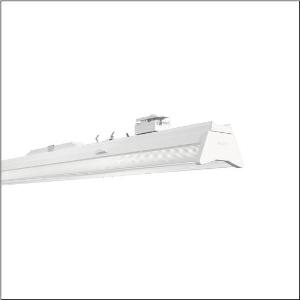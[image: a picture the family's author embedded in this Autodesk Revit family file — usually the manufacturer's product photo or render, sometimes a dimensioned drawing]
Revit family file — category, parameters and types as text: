
# Revit family: licross_r__11_performance_tw_51tm16tnt85x_6a4e
name_source: partatom
category: Lighting Fixtures
units: mm (PartAtom-declared; Revit-internal decimal feet)

## family parameters
Cut with Voids When Loaded = No
Host = Face
Light Source = No
Part Type = Normal
Room Calculation Point = No
Round Connector Dimension = Use Diameter
Shared = No

## types (1)
- --- (1 x LED 2700 K ... 6500 K, 8930 lm, 56 W, 2700K)
    Apparent Load = 56 VA
    CIE Flux Codes = 63 87 95 78 100
    Color Rendering = 80
    Color Temperature = 2700K
    Default Elevation = 1800 mm
    Description = Licross® 11 Performance TW, luminaire insert, of sheet steel, galvanised, coil coated, white, length: 1.500mm, width: 120mm, height: 123mm, LED rated luminous flux: 8.930lm, light colour: 8tw, control gear: DALI DT8, with plug, 5-pole, with phase selection, mains connection: 220..240V, AC, 50/60Hz, rated input power: 56W, halogen-free wiring, primary light control with lens, of plastic, primary optical cover: cover, of PMMA, light emission: direct/indirect distribution, primary light characteristic: symmetric, protection rating (complete): IP40, insulation class (complete): insulation class I (protective earthing), certification: CE, ENEC, VDE, UKCA, protection symbol: D if used in an environment without relevant dust loads with corresponding accessories, impact resistance: IK06, permissible ambient temperature for indoor applications: -25..+35°C, corresponds to IFS (International Featured Standards) requirements for safety and quality in the food industry, reducing of maximum allowable ambient temperature of 5°C with ceiling mounting, LABS conformity tested according to VDMA 24364:2018-05, packaging unit: 1 piece
    Height = 114 mm
    Lamp = 1 x LED 2700 K ... 6500 K
    Lamp Light Flux = 8930 lm
    Lamp Power = 56 W
    Lamp count = 1
    Length = 1500 mm
    Luminous efficacy = 159 lm/W
    Manufacturer = Siteco
    ModVariant = No
    Model = 51TM16TNT85X
    Mounting Place = Ceiling
    Mounting Type = Pendant
    Number of Poles = 1
    OnlyDefault = Yes
    Power Factor = 1
    Product Name = Licross® 11 Performance TW
    Product group = luminaire insert
    ProductGroupID = 901
    Protection Class = Protection class I
    Protection Degree = IP 40
    RLX_Detail_Level = 1
    RLX_Emergency_Light_Flux = 0 lm
    RLX_Emergency_Type = 0
    RLX_Emergency_Type_DB = No
    RlxData = <blob elided: 30497 chars, md5=cbb94868>
    Socket = socket
    Standby Power = 0 W
    System Light Flux = 8930 lm
    System Power = 56 W
    Type Comments = individual setting: CCT=2700K
    Type Image = l_1256138.jpg
    URL = http://relux.com
    VarID = @adj_016021
    Voltage = 0 V
    Weight = 0.00 kg
    Width = 120 mm

## geometry (parser evidence)
native form markers: Blend x4, Sweep x12
no freeform markers — native parametric forms only
